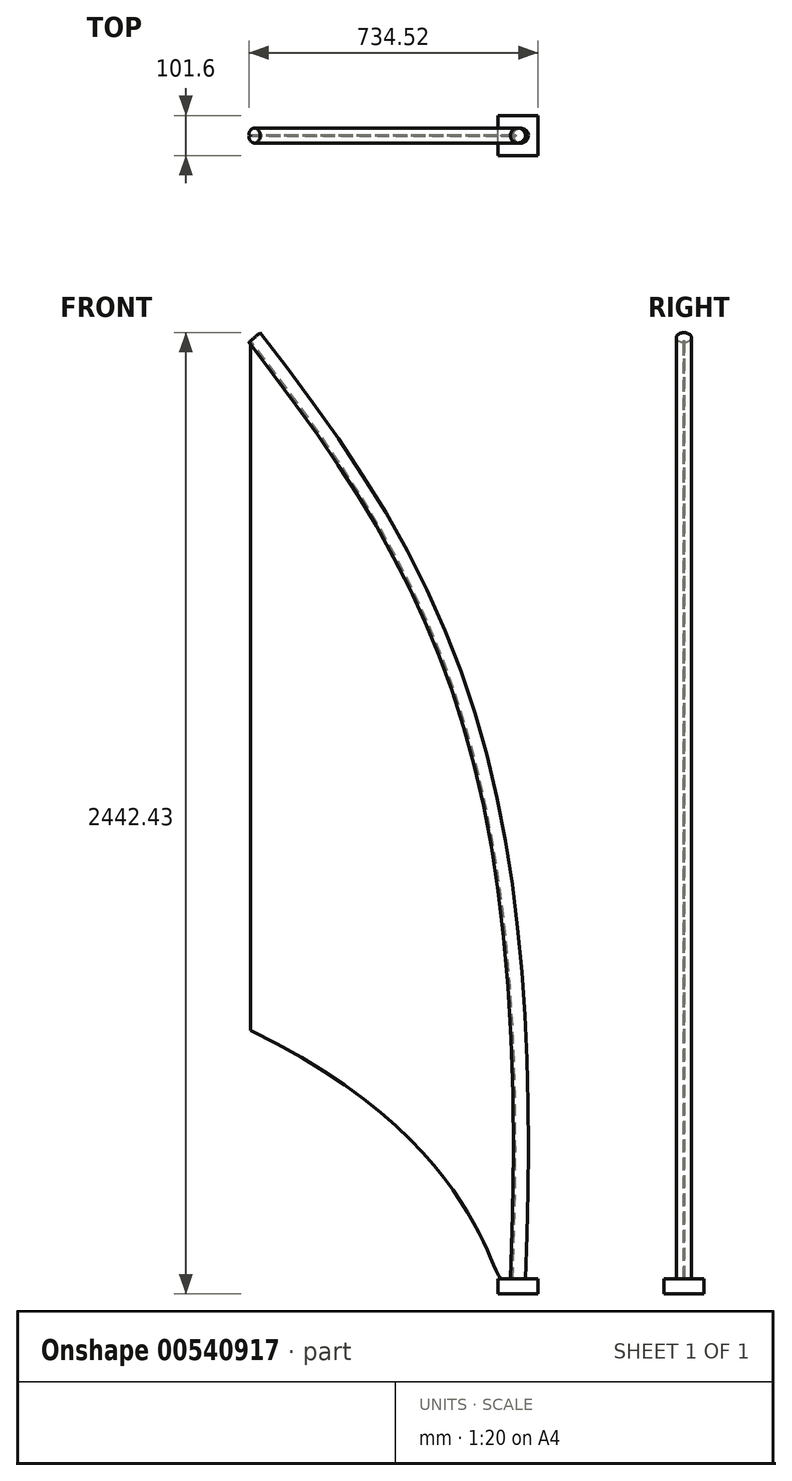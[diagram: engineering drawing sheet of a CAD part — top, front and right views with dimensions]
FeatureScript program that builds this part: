
annotation { "Feature Type Name" : "Feature", "Feature Type Description" : "" }
export const myFeature = defineFeature(function(context is Context, id is Id, definition is map)
    precondition{}
    {
        {
            var Q0;
            Q0=qCreatedBy(makeId("Front.planeOp"),FACE);
            var sketch = newSketch(context, id + "F0", { "sketchPlane" : qUnion([Q0])});
            skPoint(sketch, "E0", {"position": v(635.23, -631.27) * mm});
            skPoint(sketch, "E1", {"position": v(666.2, -631.27) * mm});
            skPoint(sketch, "E2", {"position": v(0, 1752.6) * mm});
            skLineSegment(sketch, "E3", {"start": v(0, 1752.6) * mm, "end": v(0, 0) * mm});
            skLineSegment(sketch, "E4", {"start": v(635.23, -631.27) * mm, "end": v(666.2, -631.27) * mm});
            skFitSpline(sketch, "E5", {"points": [v(0, 0) * mm, v(635.23, -631.27) * mm], "startDerivative": vector(1604.06, -779.6) * mm, "endDerivative": vector(124.44, -186.8) * mm});
            skFitSpline(sketch, "E6", {"points": [v(666.2, -631.27) * mm, v(0, 1752.6) * mm], "startDerivative": vector(161.73, 3924.3) * mm, "endDerivative": vector(-1431.38, 1847.25) * mm});
            skPoint(sketch, "E7", {"position": v(666.75, 0) * mm});
            skSolve(sketch);
        }
        {
            var Q0;
            Q0 = qSketchRegion(id + "F0", true);
            extrude(context, id + "F1", {"entities" : qUnion([Q0]), "depth" : 2.54 * mm, "offsetDistance" : 25.4 * mm});
        }
        {
            var Q0;
            Q0=makeQuery(id+"F1.opExtrude","SWEPT_FACE",FACE,{"disambiguationData":[OSD([sQuery(id+"F0.wireOp",EDGE,"E4")])]});
            var sketch = newSketch(context, id + "F2", { "sketchPlane" : qUnion([Q0])});
            skLineSegment(sketch, "E8", {"start": v(666.2, 1.27) * mm, "end": v(678.9, 1.27) * mm, "construction": true});
            skPoint(sketch, "E8.endSnap0", {"position": v(666.2, 1.27) * mm});
            skCircle(sketch, "E9", {"center": v(678.9, 1.27) * mm, "radius": 19.05 * mm});
            skSolve(sketch);
        }
        {
            var Q0;
            {var subQ1=sQuery(id+"F0.wireOp",EDGE,"E4");var subQ6=makeQuery(id+"F1.opExtrude","SWEPT_EDGE",EDGE,{"disambiguationData":[OSD([subQ1,sQuery(id+"F0.wireOp",EDGE,"E6")])]});Q0=makeQuery(id+"F2.imprint","IMPRINT",FACE,{"disambiguationData":[TD([[makeQuery(id+"F2.imprint","IMPRINT",EDGE,{"derivedFrom":subQ6}),1.0]])]});}
            var Q1;
            Q1=makeQuery(id+"F1.opExtrude","CAP_EDGE",EDGE,{"disambiguationData":[OSD([sQuery(id+"F0.wireOp",EDGE,"E6")])],"isStart":false});
            sweep(context, id + "F3", {"profiles" : qUnion([Q0]), "path" : qUnion([Q1])});
        }
        {
            var Q0;
            Q0=makeQuery(id+"F3.opSweep","CAP_FACE",FACE,{"disambiguationData":[OSD([sQuery(id+"F0.wireOp",EDGE,"E4"),sQuery(id+"F0.wireOp",EDGE,"E6"),sQuery(id+"F2.wireOp",EDGE,"E9")])],"isStart":true});
            var sketch = newSketch(context, id + "F4", { "sketchPlane" : qUnion([Q0])});
            skLineSegment(sketch, "E10.bottom", {"start": v(628.1, 52.07) * mm, "end": v(729.7, 52.07) * mm});
            skLineSegment(sketch, "E10.top", {"start": v(628.1, -49.53) * mm, "end": v(729.7, -49.53) * mm});
            skLineSegment(sketch, "E10.left", {"start": v(628.1, 52.07) * mm, "end": v(628.1, -49.53) * mm});
            skLineSegment(sketch, "E10.right", {"start": v(729.7, 52.07) * mm, "end": v(729.7, -49.53) * mm});
            skPoint(sketch, "E10.middle", {"position": v(678.9, 1.27) * mm});
            skSolve(sketch);
        }
        {
            var Q0;
            Q0 = qSketchRegion(id + "F4", true);
            extrude(context, id + "F5", {"entities" : qUnion([Q0]), "depth" : 38.1 * mm, "offsetDistance" : 25.4 * mm});
        }
    });
